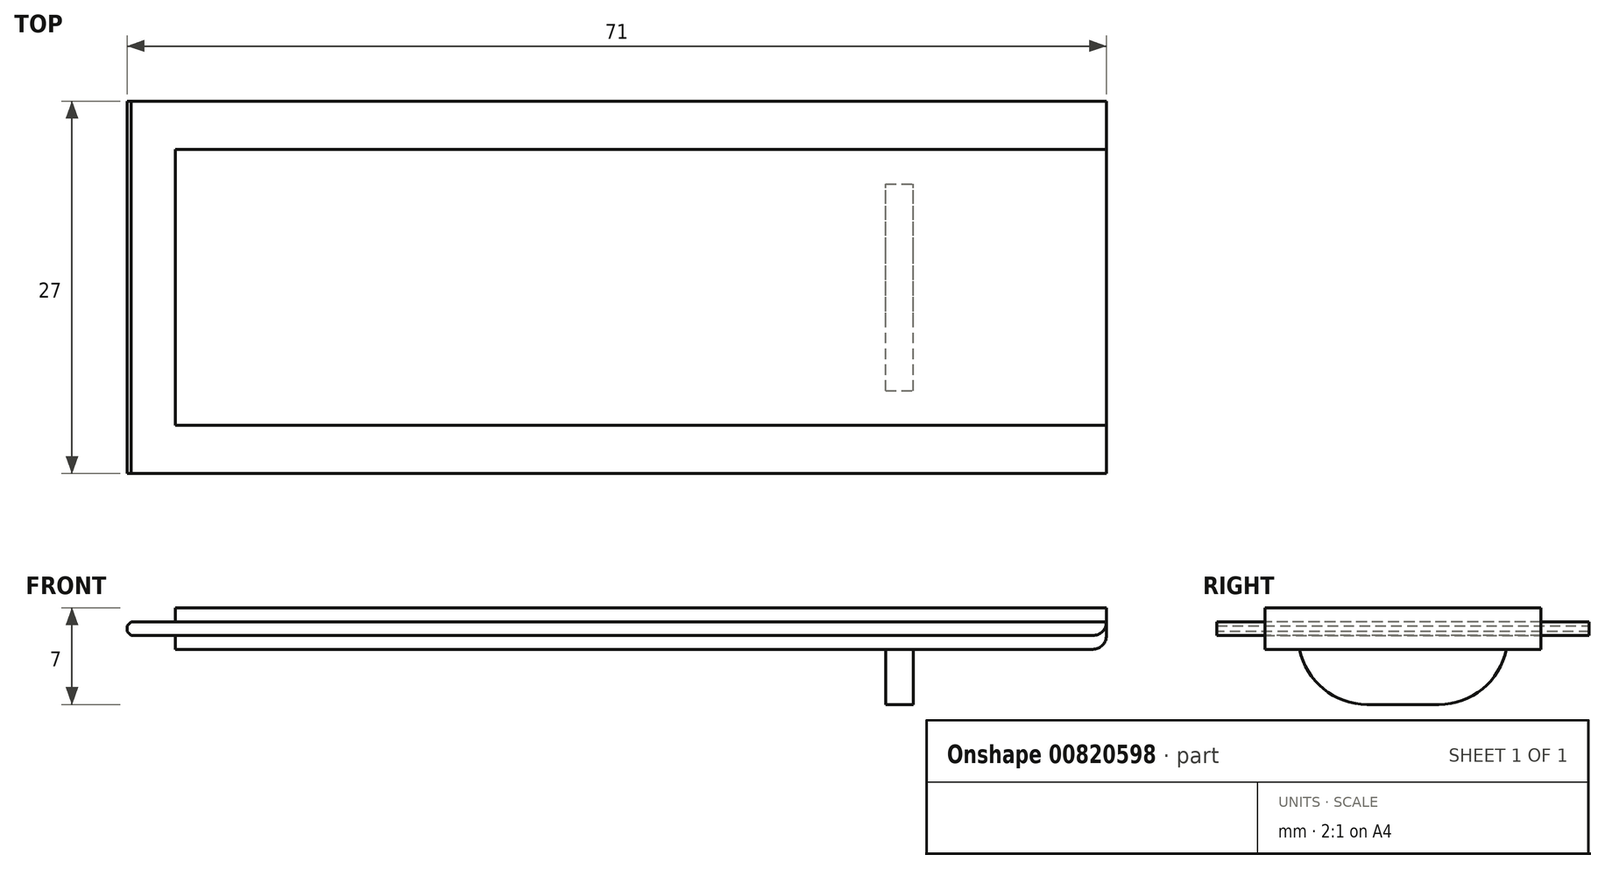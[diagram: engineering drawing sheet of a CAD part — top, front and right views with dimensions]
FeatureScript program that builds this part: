
annotation { "Feature Type Name" : "Feature", "Feature Type Description" : "" }
export const myFeature = defineFeature(function(context is Context, id is Id, definition is map)
    precondition{}
    {
        {
            var Q0;
            Q0=qCreatedBy(makeId("Top.planeOp"),FACE);
            var sketch = newSketch(context, id + "F0", { "sketchPlane" : qUnion([Q0])});
            skLineSegment(sketch, "E0.bottom", {"start": v(-37.85, -10.95) * mm, "end": v(29.65, -10.95) * mm});
            skLineSegment(sketch, "E0.top", {"start": v(-37.85, -30.95) * mm, "end": v(29.65, -30.95) * mm});
            skLineSegment(sketch, "E0.left", {"start": v(-37.85, -10.95) * mm, "end": v(-37.85, -30.95) * mm});
            skLineSegment(sketch, "E0.right", {"start": v(29.65, -10.95) * mm, "end": v(29.65, -30.95) * mm});
            skSolve(sketch);
        }
        {
            var Q0;
            Q0 = qSketchRegion(id + "F0", true);
            extrude(context, id + "F1", {"entities" : qUnion([Q0]), "depth" : 1 * mm, "offsetDistance" : 25 * mm});
        }
        {
            var Q0;
            Q0=makeQuery(id+"F1.opExtrude","CAP_FACE",FACE,{"disambiguationData":[OSD([sQuery(id+"F0.wireOp",EDGE,"E0.bottom"),sQuery(id+"F0.wireOp",EDGE,"E0.top"),sQuery(id+"F0.wireOp",EDGE,"E0.left"),sQuery(id+"F0.wireOp",EDGE,"E0.right")])],"isStart":false});
            var sketch = newSketch(context, id + "F2", { "sketchPlane" : qUnion([Q0])});
            skLineSegment(sketch, "E1.bottom", {"start": v(-41.35, -7.45) * mm, "end": v(29.65, -7.45) * mm});
            skLineSegment(sketch, "E1.top", {"start": v(-41.35, -34.45) * mm, "end": v(29.65, -34.45) * mm});
            skLineSegment(sketch, "E1.left", {"start": v(-41.35, -7.45) * mm, "end": v(-41.35, -34.45) * mm});
            skLineSegment(sketch, "E1.right", {"start": v(29.65, -7.45) * mm, "end": v(29.65, -34.45) * mm});
            skSolve(sketch);
        }
        {
            var Q0;
            Q0 = qSketchRegion(id + "F2", true);
            extrude(context, id + "F3", {"entities" : qUnion([Q0]), "operationType" : NewBodyOperationType.ADD, "depth" : 1 * mm, "offsetDistance" : 25 * mm});
        }
        {
            var Q0;
            Q0=makeQuery(id+"F3.opExtrude","CAP_FACE",FACE,{"disambiguationData":[OSD([sQuery(id+"F2.wireOp",EDGE,"E1.bottom"),sQuery(id+"F2.wireOp",EDGE,"E1.top"),sQuery(id+"F2.wireOp",EDGE,"E1.left"),sQuery(id+"F2.wireOp",EDGE,"E1.right")])],"isStart":false});
            var sketch = newSketch(context, id + "F4", { "sketchPlane" : qUnion([Q0])});
            skLineSegment(sketch, "E2.bottom", {"start": v(-37.85, -10.95) * mm, "end": v(29.65, -10.95) * mm});
            skLineSegment(sketch, "E2.top", {"start": v(-37.85, -30.95) * mm, "end": v(29.65, -30.95) * mm});
            skLineSegment(sketch, "E2.left", {"start": v(-37.85, -10.95) * mm, "end": v(-37.85, -30.95) * mm});
            skLineSegment(sketch, "E2.right", {"start": v(29.65, -10.95) * mm, "end": v(29.65, -30.95) * mm});
            skSolve(sketch);
        }
        {
            var Q0;
            Q0 = qSketchRegion(id + "F4", true);
            extrude(context, id + "F5", {"entities" : qUnion([Q0]), "operationType" : NewBodyOperationType.ADD, "depth" : 1 * mm, "offsetDistance" : 25 * mm});
        }
        {
            var Q0;
            {var subQ1=sQuery(id+"F2.wireOp",EDGE,"E1.right");Q0=makeQuery(id+"F3.boolean.opBoolean","SPLIT",EDGE,{"disambiguationData":[TD([makeQuery(id+"F1.opExtrude","SWEPT_FACE",FACE,{"disambiguationData":[OSD([sQuery(id+"F0.wireOp",EDGE,"E0.bottom")])]})])],"derivedFrom":makeQuery(id+"F3.opExtrude","CAP_EDGE",EDGE,{"disambiguationData":[OSD([subQ1])],"isStart":true})});}
            var Q1;
            {var subQ1=sQuery(id+"F2.wireOp",EDGE,"E1.right");Q1=makeQuery(id+"F3.boolean.opBoolean","SPLIT",EDGE,{"disambiguationData":[TD([makeQuery(id+"F1.opExtrude","SWEPT_FACE",FACE,{"disambiguationData":[OSD([sQuery(id+"F0.wireOp",EDGE,"E0.top")])]})])],"derivedFrom":makeQuery(id+"F3.opExtrude","CAP_EDGE",EDGE,{"disambiguationData":[OSD([subQ1])],"isStart":true})});}
            fillet(context, id + "F6", {"entities" : qUnion([Q0, Q1]), "radius" : 1 * mm, "tangentPropagation" : true, "allowEdgeOverflow" : false});
        }
        {
            var Q0;
            Q0=makeQuery(id+"F1.opExtrude","CAP_EDGE",EDGE,{"disambiguationData":[OSD([sQuery(id+"F0.wireOp",EDGE,"E0.right")])],"isStart":true});
            fillet(context, id + "F7", {"entities" : qUnion([Q0]), "radius" : 1 * mm, "tangentPropagation" : true, "allowEdgeOverflow" : false});
        }
        {
            var Q0;
            Q0=makeQuery(id+"F1.opExtrude","CAP_FACE",FACE,{"disambiguationData":[OSD([sQuery(id+"F0.wireOp",EDGE,"E0.bottom"),sQuery(id+"F0.wireOp",EDGE,"E0.top"),sQuery(id+"F0.wireOp",EDGE,"E0.left"),sQuery(id+"F0.wireOp",EDGE,"E0.right")])],"isStart":true});
            var sketch = newSketch(context, id + "F8", { "sketchPlane" : qUnion([Q0])});
            skLineSegment(sketch, "E3.bottom", {"start": v(13.65, 28.45) * mm, "end": v(15.65, 28.45) * mm});
            skLineSegment(sketch, "E3.top", {"start": v(13.65, 13.45) * mm, "end": v(15.65, 13.45) * mm});
            skLineSegment(sketch, "E3.left", {"start": v(13.65, 28.45) * mm, "end": v(13.65, 13.45) * mm});
            skLineSegment(sketch, "E3.right", {"start": v(15.65, 28.45) * mm, "end": v(15.65, 13.45) * mm});
            skSolve(sketch);
        }
        {
            var Q0;
            Q0 = qSketchRegion(id + "F8", true);
            extrude(context, id + "F9", {"entities" : qUnion([Q0]), "operationType" : NewBodyOperationType.ADD, "depth" : 4 * mm, "offsetDistance" : 25 * mm});
        }
        {
            var Q0;
            Q0=makeQuery(id+"F9.opExtrude","CAP_EDGE",EDGE,{"disambiguationData":[OSD([sQuery(id+"F8.wireOp",EDGE,"E3.bottom")])],"isStart":false});
            var Q1;
            Q1=makeQuery(id+"F9.opExtrude","CAP_EDGE",EDGE,{"disambiguationData":[OSD([sQuery(id+"F8.wireOp",EDGE,"E3.top")])],"isStart":false});
            fillet(context, id + "F10", {"entities" : qUnion([Q0, Q1]), "radius" : 5 * mm, "tangentPropagation" : true, "allowEdgeOverflow" : false});
        }
        {
            var Q0;
            Q0=makeQuery(id+"F3.opExtrude","CAP_EDGE",EDGE,{"disambiguationData":[OSD([sQuery(id+"F2.wireOp",EDGE,"E1.left")])],"isStart":false});
            var Q1;
            Q1=makeQuery(id+"F3.opExtrude","CAP_EDGE",EDGE,{"disambiguationData":[OSD([sQuery(id+"F2.wireOp",EDGE,"E1.left")])],"isStart":true});
            chamfer(context, id + "F11", {"entities" : qUnion([Q0, Q1]), "width" : 0.3 * mm, "tangentPropagation" : true});
        }
    });
